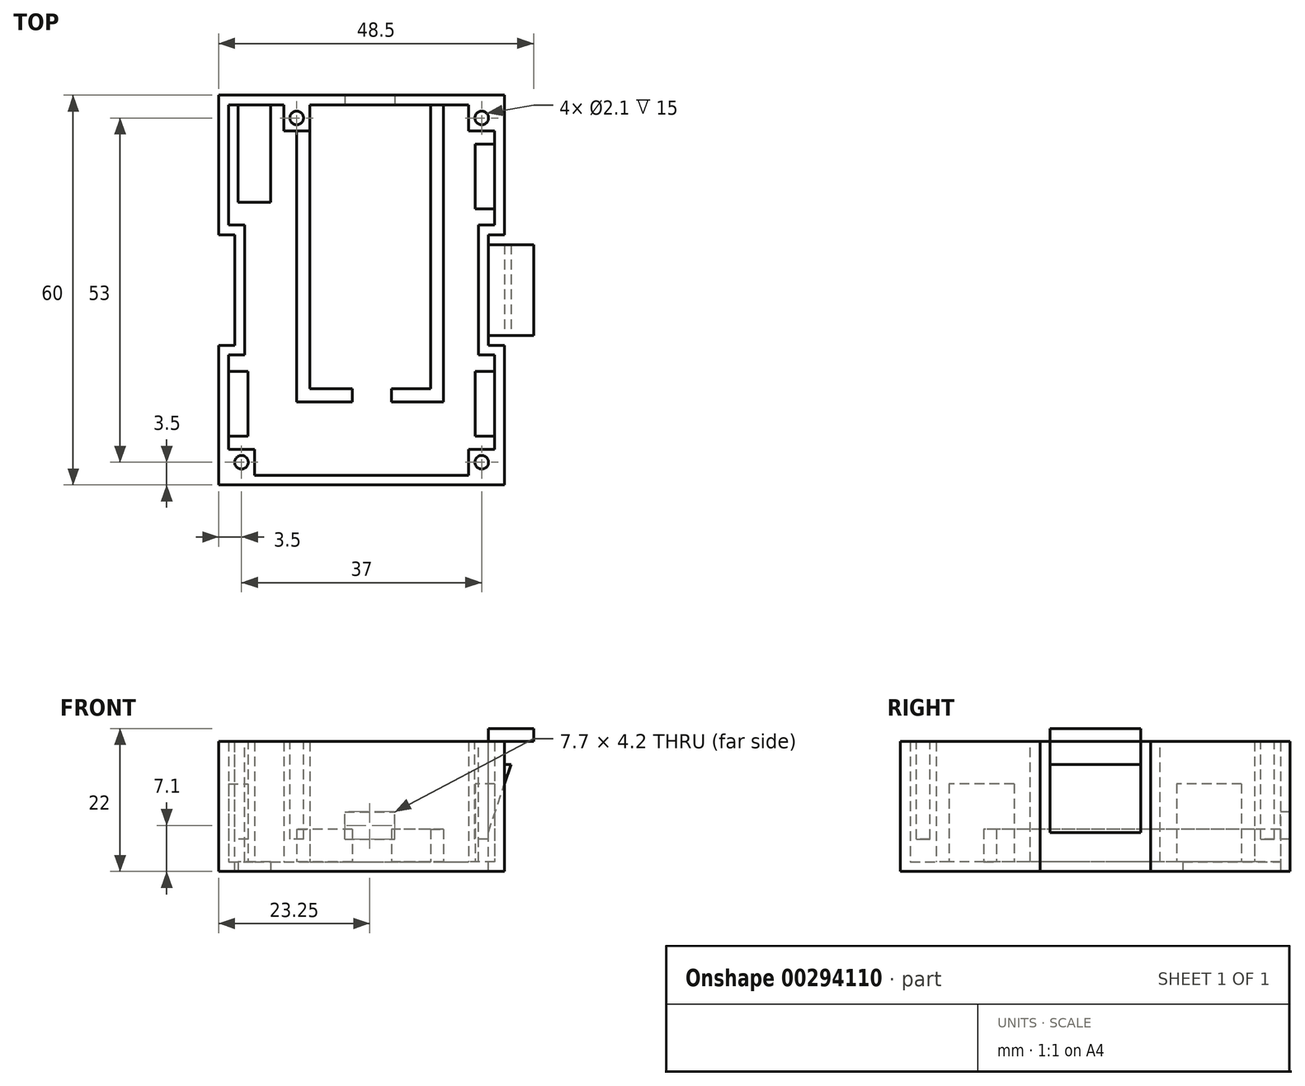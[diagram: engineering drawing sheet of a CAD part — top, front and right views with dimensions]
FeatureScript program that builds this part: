
annotation { "Feature Type Name" : "Feature", "Feature Type Description" : "" }
export const myFeature = defineFeature(function(context is Context, id is Id, definition is map)
    precondition{}
    {
        {
            var Q0;
            Q0=qCreatedBy(makeId("Top.planeOp"),FACE);
            var sketch = newSketch(context, id + "F0", { "sketchPlane" : qUnion([Q0])});
            skLineSegment(sketch, "E0.bottom", {"start": v(-22, 30) * mm, "end": v(22, 30) * mm});
            skLineSegment(sketch, "E0.top", {"start": v(-22, -30) * mm, "end": v(22, -30) * mm});
            skLineSegment(sketch, "E0.left", {"start": v(-22, 30) * mm, "end": v(-22, -30) * mm});
            skLineSegment(sketch, "E0.right", {"start": v(22, 30) * mm, "end": v(22, -30) * mm});
            skSolve(sketch);
        }
        {
            var Q0;
            Q0=qSketchRegion(id+"F0",true);
            extrude(context, id + "F1", {"entities" : qUnion([Q0]), "depth" : 20 * mm});
        }
        {
            var Q0;
            Q0=makeQuery(id+"F1.opExtrude","CAP_FACE",FACE,{"disambiguationData":[OSD([sQuery(id+"F0.wireOp",EDGE,"E0.bottom"),sQuery(id+"F0.wireOp",EDGE,"E0.top"),sQuery(id+"F0.wireOp",EDGE,"E0.left"),sQuery(id+"F0.wireOp",EDGE,"E0.right")])],"isStart":false});
            var sketch = newSketch(context, id + "F2", { "sketchPlane" : qUnion([Q0])});
            skLineSegment(sketch, "E1.bottom", {"start": v(22, 8.5) * mm, "end": v(19.5, 8.5) * mm});
            skLineSegment(sketch, "E1.top", {"start": v(22, -8.5) * mm, "end": v(19.5, -8.5) * mm});
            skLineSegment(sketch, "E1.left", {"start": v(22, 8.5) * mm, "end": v(22, -8.5) * mm});
            skLineSegment(sketch, "E1.right", {"start": v(19.5, 8.5) * mm, "end": v(19.5, -8.5) * mm});
            skLineSegment(sketch, "E2.bottom", {"start": v(-22, 8.5) * mm, "end": v(-19.5, 8.5) * mm});
            skLineSegment(sketch, "E2.top", {"start": v(-22, -8.5) * mm, "end": v(-19.5, -8.5) * mm});
            skLineSegment(sketch, "E2.left", {"start": v(-22, 8.5) * mm, "end": v(-22, -8.5) * mm});
            skLineSegment(sketch, "E2.right", {"start": v(-19.5, 8.5) * mm, "end": v(-19.5, -8.5) * mm});
            skSolve(sketch);
        }
        {
            var Q0;
            Q0=qSketchRegion(id+"F2",true);
            extrude(context, id + "F3", {"entities" : qUnion([Q0]), "operationType" : NewBodyOperationType.REMOVE, "oppositeDirection" : true, "depth" : 20 * mm});
        }
        {
            var Q0;
            Q0=makeQuery(id+"F1.opExtrude","CAP_FACE",FACE,{"disambiguationData":[OSD([sQuery(id+"F0.wireOp",EDGE,"E0.bottom"),sQuery(id+"F0.wireOp",EDGE,"E0.top"),sQuery(id+"F0.wireOp",EDGE,"E0.left"),sQuery(id+"F0.wireOp",EDGE,"E0.right")])],"isStart":false});
            shell(context, id + "F4", {"entities" : qUnion([Q0]), "thickness" : 1.5 * mm});
        }
        {
            var Q0;
            Q0=makeQuery(id+"F1.opExtrude","CAP_FACE",FACE,{"disambiguationData":[OSD([sQuery(id+"F0.wireOp",EDGE,"E0.bottom"),sQuery(id+"F0.wireOp",EDGE,"E0.top"),sQuery(id+"F0.wireOp",EDGE,"E0.left"),sQuery(id+"F0.wireOp",EDGE,"E0.right")])],"isStart":true});
            var sketch = newSketch(context, id + "F5", { "sketchPlane" : qUnion([Q0])});
            skLineSegment(sketch, "E3.bottom", {"start": v(-19, -28.5) * mm, "end": v(-14, -28.5) * mm});
            skLineSegment(sketch, "E3.top", {"start": v(-19, -13.5) * mm, "end": v(-14, -13.5) * mm});
            skLineSegment(sketch, "E3.left", {"start": v(-19, -28.5) * mm, "end": v(-19, -13.5) * mm});
            skLineSegment(sketch, "E3.right", {"start": v(-14, -28.5) * mm, "end": v(-14, -13.5) * mm});
            skSolve(sketch);
        }
        {
            var Q0;
            Q0=qSketchRegion(id+"F5",true);
            extrude(context, id + "F6", {"entities" : qUnion([Q0]), "operationType" : NewBodyOperationType.REMOVE, "oppositeDirection" : true, "depth" : 2 * mm});
        }
        {
            var Q0;
            Q0=makeQuery(id+"F3.boolean.opBoolean","COPY",FACE,{"derivedFrom":makeQuery(id+"F3.opExtrude","SWEPT_FACE",FACE,{"disambiguationData":[OSD([sQuery(id+"F2.wireOp",EDGE,"E1.right")])]})});
            var sketch = newSketch(context, id + "F7", { "sketchPlane" : qUnion([Q0])});
            skLineSegment(sketch, "E4.bottom", {"start": v(-7, 20) * mm, "end": v(7, 20) * mm});
            skLineSegment(sketch, "E4.top", {"start": v(-7, 6) * mm, "end": v(7, 6) * mm});
            skLineSegment(sketch, "E4.left", {"start": v(-7, 20) * mm, "end": v(-7, 6) * mm});
            skLineSegment(sketch, "E4.right", {"start": v(7, 20) * mm, "end": v(7, 6) * mm});
            skLineSegment(sketch, "E5.top", {"start": v(-7, 22) * mm, "end": v(7, 22) * mm});
            skLineSegment(sketch, "E5.left", {"start": v(-7, 20) * mm, "end": v(-7, 22) * mm});
            skLineSegment(sketch, "E5.right", {"start": v(7, 20) * mm, "end": v(7, 22) * mm});
            skSolve(sketch);
        }
        {
            var Q0;
            Q0=qSketchRegion(id+"F7",true);
            extrude(context, id + "F8", {"entities" : qUnion([Q0]), "operationType" : NewBodyOperationType.ADD, "depth" : 7 * mm});
        }
        {
            var Q0;
            Q0=makeQuery(id+"F8.opExtrude","SWEPT_FACE",FACE,{"disambiguationData":[OSD([sQuery(id+"F7.wireOp",EDGE,"E4.left"),sQuery(id+"F7.wireOp",EDGE,"E5.left")])]});
            var sketch = newSketch(context, id + "F9", { "sketchPlane" : qUnion([Q0])});
            skLineSegment(sketch, "E6", {"start": v(19.5, 6) * mm, "end": v(23, 16.5) * mm});
            skLineSegment(sketch, "E7", {"start": v(23, 16.5) * mm, "end": v(22, 16.5) * mm});
            skLineSegment(sketch, "E8", {"start": v(22, 16.5) * mm, "end": v(22, 20) * mm});
            skLineSegment(sketch, "E9", {"start": v(22, 20) * mm, "end": v(26.5, 20) * mm});
            skLineSegment(sketch, "E10", {"start": v(26.5, 20) * mm, "end": v(26.5, 6) * mm});
            skLineSegment(sketch, "E11", {"start": v(26.5, 6) * mm, "end": v(19.5, 6) * mm});
            skSolve(sketch);
        }
        {
            var Q0;
            Q0=qSketchRegion(id+"F9",true);
            extrude(context, id + "F10", {"entities" : qUnion([Q0]), "operationType" : NewBodyOperationType.REMOVE, "oppositeDirection" : true, "depth" : 14 * mm});
        }
        {
            var Q0;
            Q0=makeQuery(id+"F4.opShell","OFFSET_FACE",FACE,{"disambiguationData":[OSD([sQuery(id+"F0.wireOp",EDGE,"E0.bottom"),sQuery(id+"F0.wireOp",EDGE,"E0.top"),sQuery(id+"F0.wireOp",EDGE,"E0.left"),sQuery(id+"F0.wireOp",EDGE,"E0.right")])]});
            var sketch = newSketch(context, id + "F11", { "sketchPlane" : qUnion([Q0])});
            skLineSegment(sketch, "E12.bottom", {"start": v(20.5, 28.5) * mm, "end": v(16.5, 28.5) * mm});
            skLineSegment(sketch, "E12.top", {"start": v(20.5, 24.5) * mm, "end": v(16.5, 24.5) * mm});
            skLineSegment(sketch, "E12.left", {"start": v(20.5, 28.5) * mm, "end": v(20.5, 24.5) * mm});
            skLineSegment(sketch, "E12.right", {"start": v(16.5, 28.5) * mm, "end": v(16.5, 24.5) * mm});
            skLineSegment(sketch, "E13.bottom", {"start": v(20.5, -28.5) * mm, "end": v(16.5, -28.5) * mm});
            skLineSegment(sketch, "E13.top", {"start": v(20.5, -24.5) * mm, "end": v(16.5, -24.5) * mm});
            skLineSegment(sketch, "E13.left", {"start": v(20.5, -28.5) * mm, "end": v(20.5, -24.5) * mm});
            skLineSegment(sketch, "E13.right", {"start": v(16.5, -28.5) * mm, "end": v(16.5, -24.5) * mm});
            skLineSegment(sketch, "E14.bottom", {"start": v(-20.5, -28.5) * mm, "end": v(-16.5, -28.5) * mm});
            skLineSegment(sketch, "E14.top", {"start": v(-20.5, -24.5) * mm, "end": v(-16.5, -24.5) * mm});
            skLineSegment(sketch, "E14.left", {"start": v(-20.5, -28.5) * mm, "end": v(-20.5, -24.5) * mm});
            skLineSegment(sketch, "E14.right", {"start": v(-16.5, -28.5) * mm, "end": v(-16.5, -24.5) * mm});
            skLineSegment(sketch, "E15.bottom", {"start": v(-12, 28.5) * mm, "end": v(-8, 28.5) * mm});
            skLineSegment(sketch, "E15.top", {"start": v(-12, 24.5) * mm, "end": v(-8, 24.5) * mm});
            skLineSegment(sketch, "E15.left", {"start": v(-12, 28.5) * mm, "end": v(-12, 24.5) * mm});
            skLineSegment(sketch, "E15.right", {"start": v(-8, 28.5) * mm, "end": v(-8, 24.5) * mm});
            skSolve(sketch);
        }
        {
            var Q0;
            Q0=qSketchRegion(id+"F11",true);
            var Q1;
            Q1=makeQuery(id+"F1.opExtrude","CAP_FACE",FACE,{"disambiguationData":[OSD([sQuery(id+"F0.wireOp",EDGE,"E0.bottom"),sQuery(id+"F0.wireOp",EDGE,"E0.top"),sQuery(id+"F0.wireOp",EDGE,"E0.left"),sQuery(id+"F0.wireOp",EDGE,"E0.right")])],"isStart":false});
            extrude(context, id + "F12", {"entities" : qUnion([Q0]), "operationType" : NewBodyOperationType.ADD, "endBound" : BoundingType.UP_TO_SURFACE, "endBoundEntityFace" : qUnion([Q1]), "depth" : 18.5 * mm});
        }
        {
            var Q0;
            Q0=makeQuery(id+"F12.boolean.opBoolean","MERGE",FACE,{"derivedFrom":[makeQuery(id+"F1.opExtrude","CAP_FACE",FACE,{"disambiguationData":[OSD([sQuery(id+"F0.wireOp",EDGE,"E0.bottom"),sQuery(id+"F0.wireOp",EDGE,"E0.top"),sQuery(id+"F0.wireOp",EDGE,"E0.left"),sQuery(id+"F0.wireOp",EDGE,"E0.right")])],"isStart":false}),makeQuery(id+"F12.opExtrude","CAP_FACE",FACE,{"disambiguationData":[OSD([sQuery(id+"F11.wireOp",EDGE,"E12.bottom"),sQuery(id+"F11.wireOp",EDGE,"E12.top"),sQuery(id+"F11.wireOp",EDGE,"E12.left"),sQuery(id+"F11.wireOp",EDGE,"E12.right")])],"isStart":false}),makeQuery(id+"F12.opExtrude","CAP_FACE",FACE,{"disambiguationData":[OSD([sQuery(id+"F11.wireOp",EDGE,"E13.bottom"),sQuery(id+"F11.wireOp",EDGE,"E13.top"),sQuery(id+"F11.wireOp",EDGE,"E13.left"),sQuery(id+"F11.wireOp",EDGE,"E13.right")])],"isStart":false}),makeQuery(id+"F12.opExtrude","CAP_FACE",FACE,{"disambiguationData":[OSD([sQuery(id+"F11.wireOp",EDGE,"E14.bottom"),sQuery(id+"F11.wireOp",EDGE,"E14.top"),sQuery(id+"F11.wireOp",EDGE,"E14.left"),sQuery(id+"F11.wireOp",EDGE,"E14.right")])],"isStart":false}),makeQuery(id+"F12.opExtrude","CAP_FACE",FACE,{"disambiguationData":[OSD([sQuery(id+"F11.wireOp",EDGE,"E15.bottom"),sQuery(id+"F11.wireOp",EDGE,"E15.top"),sQuery(id+"F11.wireOp",EDGE,"E15.left"),sQuery(id+"F11.wireOp",EDGE,"E15.right")])],"isStart":false})]});
            var sketch = newSketch(context, id + "F13", { "sketchPlane" : qUnion([Q0])});
            skCircle(sketch, "E16", {"center": v(-10, 26.5) * mm, "radius": 1.05 * mm});
            skPoint(sketch, "E16.centerSnap0", {"position": v(-12, 26.5) * mm});
            skCircle(sketch, "E17", {"center": v(18.5, 26.5) * mm, "radius": 1.05 * mm});
            skPoint(sketch, "E17.centerSnap0", {"position": v(18.5, 24.5) * mm});
            skPoint(sketch, "E17.centerSnap1", {"position": v(16.5, 26.5) * mm});
            skCircle(sketch, "E18", {"center": v(18.5, -26.5) * mm, "radius": 1.05 * mm});
            skPoint(sketch, "E18.centerSnap0", {"position": v(16.5, -26.5) * mm});
            skPoint(sketch, "E18.centerSnap1", {"position": v(18.5, -24.5) * mm});
            skCircle(sketch, "E19", {"center": v(-18.5, -26.5) * mm, "radius": 1.05 * mm});
            skPoint(sketch, "E19.centerSnap0", {"position": v(-16.5, -26.5) * mm});
            skPoint(sketch, "E19.centerSnap1", {"position": v(-18.5, -24.5) * mm});
            skPoint(sketch, "E20", {"position": v(-10, 24.5) * mm});
            skSolve(sketch);
        }
        {
            var Q0;
            Q0=qSketchRegion(id+"F13",true);
            extrude(context, id + "F14", {"entities" : qUnion([Q0]), "operationType" : NewBodyOperationType.REMOVE, "oppositeDirection" : true, "depth" : 15 * mm});
        }
        {
            var Q0;
            {var subQ0=sQuery(id+"F11.wireOp",EDGE,"E12.right");var subQ4=sQuery(id+"F0.wireOp",EDGE,"E0.bottom");Q0=makeQuery(id+"F12.boolean.opBoolean","SPLIT",FACE,{"disambiguationData":[TD([makeQuery(id+"F12.opExtrude","SWEPT_FACE",FACE,{"disambiguationData":[OSD([subQ0])]})])],"derivedFrom":makeQuery(id+"F6.boolean.opBoolean","MERGE",FACE,{"derivedFrom":[makeQuery(id+"F4.opShell","OFFSET_FACE",FACE,{"disambiguationData":[OSD([subQ4])]})],"fromTools":[makeQuery(id+"F6.opExtrude","SWEPT_FACE",FACE,{"disambiguationData":[OSD([sQuery(id+"F5.wireOp",EDGE,"E3.bottom")])]})]})});}
            var sketch = newSketch(context, id + "F15", { "sketchPlane" : qUnion([Q0])});
            skLineSegment(sketch, "E21.bottom", {"start": v(-2.6, 5) * mm, "end": v(5.1, 5) * mm});
            skLineSegment(sketch, "E21.top", {"start": v(-2.6, 9.2) * mm, "end": v(5.1, 9.2) * mm});
            skLineSegment(sketch, "E21.left", {"start": v(-2.6, 5) * mm, "end": v(-2.6, 9.2) * mm});
            skLineSegment(sketch, "E21.right", {"start": v(5.1, 5) * mm, "end": v(5.1, 9.2) * mm});
            skSolve(sketch);
        }
        {
            var Q0;
            Q0=qSketchRegion(id+"F15",true);
            extrude(context, id + "F16", {"entities" : qUnion([Q0]), "operationType" : NewBodyOperationType.REMOVE, "endBound" : BoundingType.UP_TO_NEXT, "oppositeDirection" : true, "depth" : 25 * mm});
        }
        {
            var Q0;
            Q0=makeQuery(id+"F4.opShell","OFFSET_FACE",FACE,{"disambiguationData":[OSD([sQuery(id+"F0.wireOp",EDGE,"E0.bottom"),sQuery(id+"F0.wireOp",EDGE,"E0.top"),sQuery(id+"F0.wireOp",EDGE,"E0.left"),sQuery(id+"F0.wireOp",EDGE,"E0.right")])]});
            var sketch = newSketch(context, id + "F17", { "sketchPlane" : qUnion([Q0])});
            skLineSegment(sketch, "E22.bottom", {"start": v(10.6, 28.5) * mm, "end": v(12.6, 28.5) * mm});
            skLineSegment(sketch, "E22.top", {"start": v(10.6, -15.2) * mm, "end": v(12.6, -15.2) * mm});
            skLineSegment(sketch, "E22.left", {"start": v(10.6, 28.5) * mm, "end": v(10.6, -15.2) * mm});
            skLineSegment(sketch, "E22.right", {"start": v(12.6, 28.5) * mm, "end": v(12.6, -15.2) * mm});
            skLineSegment(sketch, "E23.bottom", {"start": v(-8, 24.5) * mm, "end": v(-10, 24.5) * mm});
            skLineSegment(sketch, "E23.top", {"start": v(-8, -15.2) * mm, "end": v(-10, -15.2) * mm});
            skLineSegment(sketch, "E23.left", {"start": v(-8, 24.5) * mm, "end": v(-8, -15.2) * mm});
            skLineSegment(sketch, "E23.right", {"start": v(-10, 24.5) * mm, "end": v(-10, -15.2) * mm});
            skLineSegment(sketch, "E24.bottom", {"start": v(12.6, -15.2) * mm, "end": v(-10, -15.2) * mm});
            skLineSegment(sketch, "E24.top", {"start": v(12.6, -17.2) * mm, "end": v(-10, -17.2) * mm});
            skLineSegment(sketch, "E24.left", {"start": v(12.6, -15.2) * mm, "end": v(12.6, -17.2) * mm});
            skLineSegment(sketch, "E24.right", {"start": v(-10, -15.2) * mm, "end": v(-10, -17.2) * mm});
            skSolve(sketch);
        }
        {
            var Q0;
            Q0=qSketchRegion(id+"F17",true);
            extrude(context, id + "F18", {"entities" : qUnion([Q0]), "operationType" : NewBodyOperationType.ADD, "depth" : 5 * mm});
        }
        {
            var Q0;
            {var subQ2=sQuery(id+"F0.wireOp",EDGE,"E0.right");var subQ3=sQuery(id+"F0.wireOp",EDGE,"E0.left");var subQ4=sQuery(id+"F0.wireOp",EDGE,"E0.top");var subQ5=sQuery(id+"F0.wireOp",EDGE,"E0.bottom");Q0=makeQuery(id+"F18.boolean.opBoolean","SPLIT",FACE,{"disambiguationData":[TD([makeQuery(id+"F4.opShell","OFFSET_FACE",FACE,{"disambiguationData":[OSD([subQ4])]})])],"derivedFrom":makeQuery(id+"F4.opShell","OFFSET_FACE",FACE,{"disambiguationData":[OSD([subQ5,subQ4,subQ3,subQ2])]})});}
            var sketch = newSketch(context, id + "F19", { "sketchPlane" : qUnion([Q0])});
            skLineSegment(sketch, "E25.bottom", {"start": v(20.5, 22.5) * mm, "end": v(17.5, 22.5) * mm});
            skLineSegment(sketch, "E25.top", {"start": v(20.5, 12.5) * mm, "end": v(17.5, 12.5) * mm});
            skLineSegment(sketch, "E25.left", {"start": v(20.5, 22.5) * mm, "end": v(20.5, 12.5) * mm});
            skLineSegment(sketch, "E25.right", {"start": v(17.5, 22.5) * mm, "end": v(17.5, 12.5) * mm});
            skLineSegment(sketch, "E26.bottom", {"start": v(20.5, -12.5) * mm, "end": v(17.5, -12.5) * mm});
            skLineSegment(sketch, "E26.top", {"start": v(20.5, -22.5) * mm, "end": v(17.5, -22.5) * mm});
            skLineSegment(sketch, "E26.left", {"start": v(20.5, -12.5) * mm, "end": v(20.5, -22.5) * mm});
            skLineSegment(sketch, "E26.right", {"start": v(17.5, -12.5) * mm, "end": v(17.5, -22.5) * mm});
            skLineSegment(sketch, "E27.bottom", {"start": v(-20.5, -12.5) * mm, "end": v(-17.5, -12.5) * mm});
            skLineSegment(sketch, "E27.top", {"start": v(-20.5, -22.5) * mm, "end": v(-17.5, -22.5) * mm});
            skLineSegment(sketch, "E27.left", {"start": v(-20.5, -12.5) * mm, "end": v(-20.5, -22.5) * mm});
            skLineSegment(sketch, "E27.right", {"start": v(-17.5, -12.5) * mm, "end": v(-17.5, -22.5) * mm});
            skSolve(sketch);
        }
        {
            var Q0;
            Q0=qSketchRegion(id+"F19",true);
            extrude(context, id + "F20", {"entities" : qUnion([Q0]), "operationType" : NewBodyOperationType.ADD, "depth" : 12 * mm});
        }
        {
            var Q0;
            {var subQ2=sQuery(id+"F0.wireOp",EDGE,"E0.right");var subQ3=sQuery(id+"F0.wireOp",EDGE,"E0.left");var subQ4=sQuery(id+"F0.wireOp",EDGE,"E0.top");var subQ5=sQuery(id+"F0.wireOp",EDGE,"E0.bottom");Q0=makeQuery(id+"F18.boolean.opBoolean","SPLIT",FACE,{"disambiguationData":[TD([makeQuery(id+"F4.opShell","OFFSET_FACE",FACE,{"disambiguationData":[OSD([subQ4])]})])],"derivedFrom":makeQuery(id+"F4.opShell","OFFSET_FACE",FACE,{"disambiguationData":[OSD([subQ5,subQ4,subQ3,subQ2])]})});}
            var sketch = newSketch(context, id + "F21", { "sketchPlane" : qUnion([Q0])});
            skLineSegment(sketch, "E28.bottom", {"start": v(-1.4, -17.2) * mm, "end": v(4.6, -17.2) * mm});
            skLineSegment(sketch, "E28.top", {"start": v(-1.4, -15.2) * mm, "end": v(4.6, -15.2) * mm});
            skLineSegment(sketch, "E28.left", {"start": v(-1.4, -17.2) * mm, "end": v(-1.4, -15.2) * mm});
            skLineSegment(sketch, "E28.right", {"start": v(4.6, -17.2) * mm, "end": v(4.6, -15.2) * mm});
            skSolve(sketch);
        }
        {
            var Q0;
            Q0=qSketchRegion(id+"F21",true);
            extrude(context, id + "F22", {"entities" : qUnion([Q0]), "operationType" : NewBodyOperationType.REMOVE, "depth" : 10 * mm});
        }
    });
